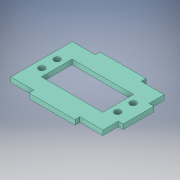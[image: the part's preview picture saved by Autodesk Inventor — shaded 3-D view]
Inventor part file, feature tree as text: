
AUTODESK INVENTOR PART (.ipt)
format: ipt  version: 2019 (Build 230136000, 136)  size: 155,136 bytes
history: native  units: mm
features: other x1, extrude x1, sketch x1
ambient origin geometry x8: Origin, YZ Plane, XZ Plane, XY Plane, X Axis, Y Axis, Z Axis, Center Point
bodies: Body1 (feature_tree)
feature tree (3):
  other  "Sólido1"
  extrude  "Extrusión1"  Depth=40.0mm
  sketch  "Boceto1"  dims[d0=10.0mm d1=10.0mm d2=20.0mm d3=10.1mm d4=40.0mm d5=4.0mm d6=4.0mm d7=4.0mm d8=5.0mm d9=10.0mm d10=14.85mm d11=14.85mm d12=4.0mm d13=34.66mm d14=34.66mm d15=5.0mm d16=10.0mm d25=40.0mm d26=60.0mm d27=20.0mm d28=20.0mm d29=3.18mm d30=30.0mm d31=15.0mm d32=20.0mm d33=10.0mm d34=3.18mm d35=3.18mm d36=0.0mm]
